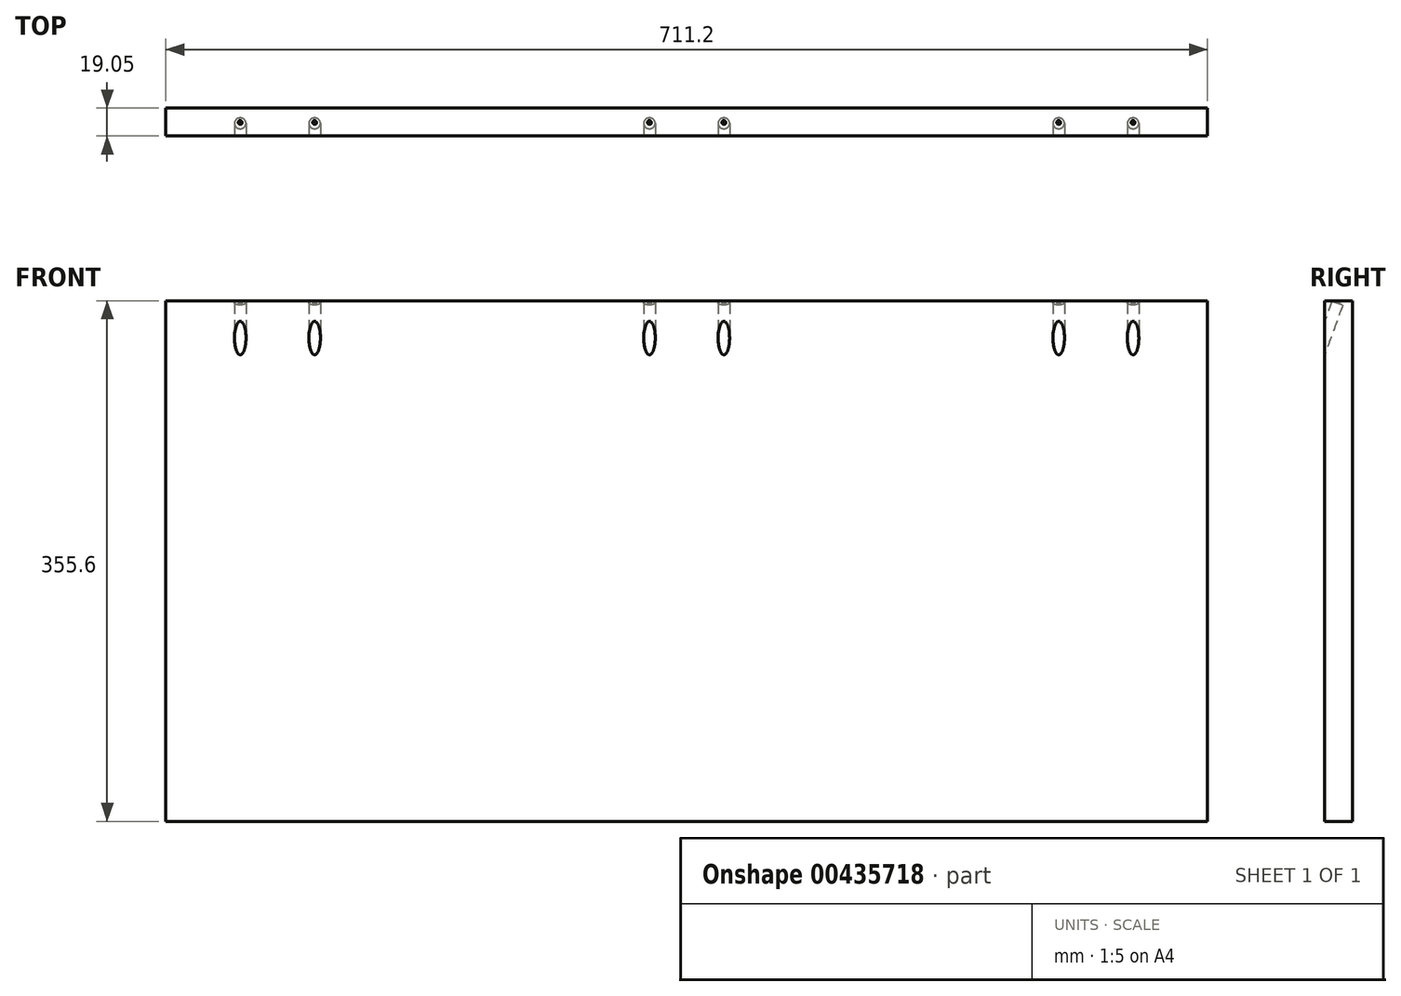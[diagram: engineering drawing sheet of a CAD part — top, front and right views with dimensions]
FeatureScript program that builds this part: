
annotation { "Feature Type Name" : "Feature", "Feature Type Description" : "" }
export const myFeature = defineFeature(function(context is Context, id is Id, definition is map)
    precondition{}
    {
        {
            var Q0;
            Q0=qCreatedBy(makeId("Front.planeOp"),FACE);
            var sketch = newSketch(context, id + "F0", { "sketchPlane" : qUnion([Q0])});
            skLineSegment(sketch, "E0.bottom", {"start": v(0, 0) * mm, "end": v(711.2, 0) * mm});
            skLineSegment(sketch, "E0.top", {"start": v(0, 355.6) * mm, "end": v(711.2, 355.6) * mm});
            skLineSegment(sketch, "E0.left", {"start": v(0, 0) * mm, "end": v(0, 355.6) * mm});
            skLineSegment(sketch, "E0.right", {"start": v(711.2, 0) * mm, "end": v(711.2, 355.6) * mm});
            skSolve(sketch);
        }
        {
            var Q0;
            Q0 = qSketchRegion(id + "F0", true);
            extrude(context, id + "F1", {"entities" : qUnion([Q0]), "depth" : 19.05 * mm});
        }
        {
            var Q0;
            Q0=makeQuery(id+"F1.opExtrude","CAP_FACE",FACE,{"disambiguationData":[OSD([sQuery(id+"F0.wireOp",EDGE,"E0.bottom"),sQuery(id+"F0.wireOp",EDGE,"E0.top"),sQuery(id+"F0.wireOp",EDGE,"E0.left"),sQuery(id+"F0.wireOp",EDGE,"E0.right")])],"isStart":false});
            var sketch = newSketch(context, id + "F2", { "sketchPlane" : qUnion([Q0])});
            skLineSegment(sketch, "E1", {"start": v(0, 330.2) * mm, "end": v(711.2, 330.2) * mm});
            skSolve(sketch);
        }
        {
            var Q0;
            Q0=sQuery(id+"F2.wireOp",EDGE,"E1");
            var Q1;
            {var subQ0=sQuery(id+"F2.wireOp",EDGE,"E1");Q1=makeQuery(id+"F2.imprint","IMPRINT",FACE,{"disambiguationData":[TD([[makeQuery(id+"F2.imprint","IMPRINT",EDGE,{"derivedFrom":subQ0}),-1.0]])]});}
            cPlane(context, id + "F3", {"entities" : qUnion([Q0, Q1]), "cplaneType" : CPlaneType.LINE_ANGLE, "offset" : 25.4 * mm, "angle" : 70 * degree, "width" : 152.4 * mm, "height" : 152.4 * mm});
        }
        {
            var Q0;
            Q0=qCreatedBy(id+"F3.planeOp",FACE);
            var sketch = newSketch(context, id + "F4", { "sketchPlane" : qUnion([Q0])});
            skLineSegment(sketch, "E2.0", {"start": v(0, -130.84) * mm, "end": v(711.2, -130.84) * mm});
            skCircle(sketch, "E3", {"center": v(50.8, -130.84) * mm, "radius": 3.94 * mm});
            skCircle(sketch, "E4", {"center": v(101.6, -130.84) * mm, "radius": 3.94 * mm});
            skCircle(sketch, "E5", {"center": v(660.4, -130.84) * mm, "radius": 3.94 * mm});
            skCircle(sketch, "E6", {"center": v(609.6, -130.84) * mm, "radius": 3.94 * mm});
            skCircle(sketch, "E7", {"center": v(381, -130.84) * mm, "radius": 3.94 * mm});
            skCircle(sketch, "E8", {"center": v(330.2, -130.84) * mm, "radius": 3.94 * mm});
            skLineSegment(sketch, "E9", {"start": v(355.6, -130.84) * mm, "end": v(405.93, -107.1) * mm});
            skSolve(sketch);
        }
        {
            var Q0;
            Q0 = qSketchRegion(id + "F4", true);
            extrude(context, id + "F5", {"entities" : qUnion([Q0]), "operationType" : NewBodyOperationType.REMOVE, "endBound" : BoundingType.SYMMETRIC, "depth" : 50.8 * mm});
        }
        {
            var Q0;
            Q0=makeQuery(id+"F5.boolean.opBoolean","COPY",FACE,{"derivedFrom":makeQuery(id+"F5.opExtrude","CAP_FACE",FACE,{"disambiguationData":[OSD([sQuery(id+"F4.wireOp",EDGE,"E3")])],"isStart":false})});
            var sketch = newSketch(context, id + "F6", { "sketchPlane" : qUnion([Q0])});
            skCircle(sketch, "E10.0", {"center": v(50.8, 130.84) * mm, "radius": 3.94 * mm});
            skCircle(sketch, "E11.0", {"center": v(101.6, 130.84) * mm, "radius": 3.94 * mm});
            skCircle(sketch, "E12.0", {"center": v(330.2, 130.84) * mm, "radius": 3.94 * mm});
            skCircle(sketch, "E13.0", {"center": v(381, 130.84) * mm, "radius": 3.94 * mm});
            skCircle(sketch, "E14.0", {"center": v(660.4, 130.84) * mm, "radius": 3.94 * mm});
            skCircle(sketch, "E15.0", {"center": v(609.6, 130.84) * mm, "radius": 3.94 * mm});
            skSolve(sketch);
        }
        {
            var Q0;
            Q0=sQuery(id+"F6.wireOp",VERTEX,"E14.0.center");
            var Q1;
            Q1=sQuery(id+"F6.wireOp",VERTEX,"E15.0.center");
            var Q2;
            Q2=sQuery(id+"F6.wireOp",VERTEX,"E13.0.center");
            var Q3;
            Q3=sQuery(id+"F6.wireOp",VERTEX,"E12.0.center");
            var Q4;
            Q4=sQuery(id+"F6.wireOp",VERTEX,"E11.0.center");
            var Q5;
            Q5=sQuery(id+"F6.wireOp",VERTEX,"E10.0.center");
            var Q6;
            Q6=makeQuery(id+"F1.opExtrude","SWEPT_BODY",BODY,{"disambiguationData":[OSD([sQuery(id+"F0.wireOp",EDGE,"E0.bottom"),sQuery(id+"F0.wireOp",EDGE,"E0.top"),sQuery(id+"F0.wireOp",EDGE,"E0.left"),sQuery(id+"F0.wireOp",EDGE,"E0.right")])]});
            hole(context, id + "F7", {"style" : HoleStyle.SIMPLE, "endStyle" : HoleEndStyle.THROUGH, "holeDiameter" : 2.54 * mm, "isTappedThrough" : true, "tappedDepth" : 12.7 * mm, "tapClearance" : 3, "locations" : qUnion([Q0, Q1, Q2, Q3, Q4, Q5]), "scope" : qUnion([Q6])});
        }
        {
            var Q0;
            Q0=makeQuery(id+"F1.opExtrude","SWEPT_FACE",FACE,{"disambiguationData":[OSD([sQuery(id+"F0.wireOp",EDGE,"E0.top")])]});
            var Q1;
            Q1=makeQuery(id+"F1.opExtrude","SWEPT_FACE",FACE,{"disambiguationData":[OSD([sQuery(id+"F0.wireOp",EDGE,"E0.bottom")])]});
            cPlane(context, id + "F8", {"entities" : qUnion([Q0, Q1]), "cplaneType" : CPlaneType.MID_PLANE, "offset" : 25.4 * mm, "width" : 152.4 * mm, "height" : 152.4 * mm});
        }
    });
